# Revit family: 0045170+0045231 Feilo Sylvania Lighting Fixture SYLBATTEN LED1 NW TP3 with SYMMETRIC REFLECTOR ACCESSORY 600MM
name_source: partatom
category: Lighting Fixtures
revit_build: Autodesk Revit 2017 (Build: 20190507_1515(x64)
units: mm (PartAtom-declared; Revit-internal decimal feet)

## family parameters
Cut with Voids When Loaded = No
Host = Face
Light Source = Yes
OmniClass Number = 23.80.70.00
OmniClass Title = Lighting
Part Type = Normal
Room Calculation Point = No
Round Connector Dimension = Use Diameter
Shared = No

## types (1)
- 0045170 SYLBATTEN LED1 NW TP3
    Apparent Load = 11 VA
    Assembly Code = D5020200
    AssetType = Fixed
    AsymReflector_FEILO = No
    BackReflector_FEILO = Yes
    CapOffset_FEILO = 2 mm  [stored 0.00656168 ft]
    ClassificationName = Uniclass2015
    ClassificationValue = EF_70_80
    Color Filter = 16777215
    Cost = 0 $
    Default Elevation = 1219 mm
    Description = LED batten, T8 replacement, ease of installation through 2 part push-in design of the housing (safety cable included), through wiring capability (TP3 = 3 core), sheet steel, 1158LM, 11W, 105lm/W, 4000K, drive current: 350mA, CRI 80, 138° wide beam angle, electronic driver (non dimmable), IP20, IK07, 50,000 hrs (L70), (LxWxH) 605x66x76mm, 5 step MacAdam ellipse, 1.8kg, white RAL9016, Class 1, 220-240V, energy class: A++, A+, A.
    Dimming Lamp Color Temperature Shift = <None>
    DocumentationLiterature = http://www.sylvania-lighting.com
    DurationUnit = hours
    ElectricShockClassification = Class I
    Emit Shape Visible in Rendering = No
    Emit from Rectangle Length = 26 mm
    Emit from Rectangle Width = 589 mm
    ExpectedLife = 50000
    FrontReflector_FEILO = Yes
    Height_FEILO = 76 mm  [stored 0.249344 ft]
    IfcExportAs = IfcLightFixtureType
    IfcExportType = IfcLightFixtureType
    ImpactProtectionIndex = IK07
    IngressProtection = IP20
    InputVoltage = 220-240V~
    Keynote = 16500
    Lamp = LED
    LampColourRenderingIndex = 80
    LampColourTemperature = 4000 K
    LampNominalLuminous = 1158 lm
    LampsType = LED
    Length_FEILO = 605 mm  [stored 1.98491 ft]
    LightOutputRatio = 100
    LuminousEfficacy = 105.2 lm/W
    Manufacturer = Feilo Sylvania
    ManufacturerName = Feilo Sylvania
    Material = sheet steel housing, polycarbonate diffuser
    Material_1_FEILO = Body-Sylvania-Sylbatten-White
    Material_2_FEILO = Body-Sylvania-Sylbatten-White
    Material_3_FEILO = Diffuser-Sylvania-Sylbatten-Glow
    Material_4_FEILO = Reflector-Sylvania-Sylbatten-White
    Model = SYLBATTEN LED1 NW TP3
    ModelNumber = 0045170
    ModelReference = SYLBATTEN LED1 NW TP3
    Name = SYLBATTEN LED1 NW TP3
    NominalDepth = 122 mm
    NominalHeight = 91 mm
    NominalLength = 605 mm  [stored 1.98491 ft]
    Photometric Web File = 0045170+0045231.ies
    PowerConsumption = 11 W
    PowerFactor = 0
    SymReflector_FEILO = Yes
    Tilt Angle = -90.00°
    Type Image = <None>
    TypeName = SYLBATTEN LED1 NW TP3
    URL = http://www.sylvania-lighting.com
    Voltage = 230 V
    Weight = 1.244 kg
    Width_FEILO = 66 mm  [stored 0.216535 ft]

note: [stored X ft] marks values corroborated as IEEE doubles in the binary element streams (Revit-internal decimal feet)
